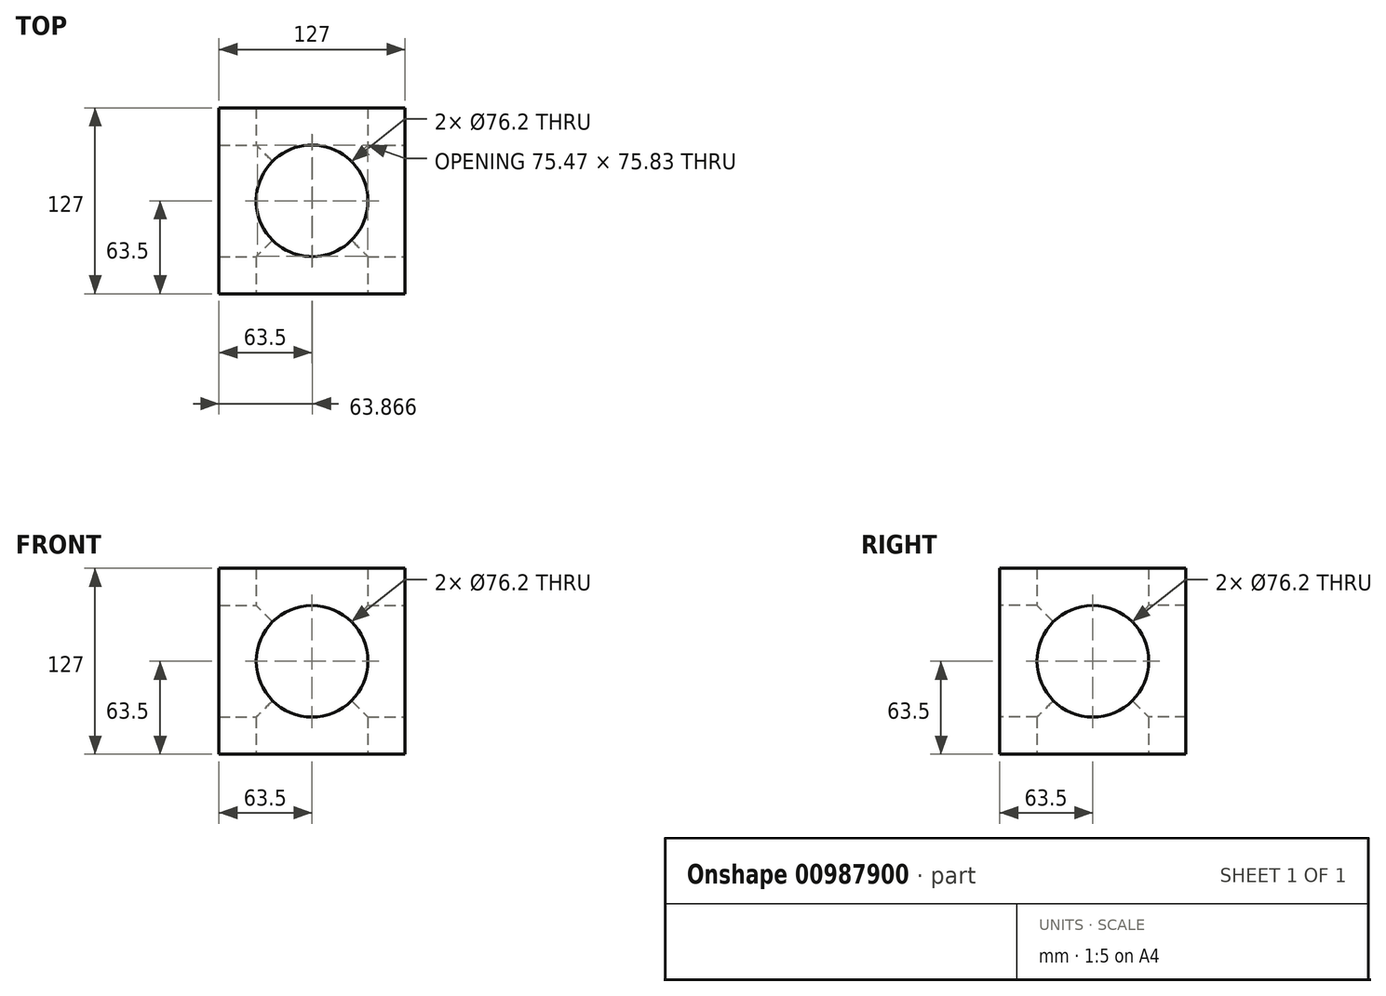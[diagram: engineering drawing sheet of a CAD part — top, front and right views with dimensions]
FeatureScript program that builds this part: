
annotation { "Feature Type Name" : "Feature", "Feature Type Description" : "" }
export const myFeature = defineFeature(function(context is Context, id is Id, definition is map)
    precondition{}
    {
        {
            var Q0;
            Q0=qCreatedBy(makeId("Top.planeOp"),FACE);
            var sketch = newSketch(context, id + "F0", { "sketchPlane" : qUnion([Q0])});
            skLineSegment(sketch, "E0.bottom", {"start": v(63.5, -63.5) * mm, "end": v(-63.5, -63.5) * mm});
            skLineSegment(sketch, "E0.top", {"start": v(63.5, 63.5) * mm, "end": v(-63.5, 63.5) * mm});
            skLineSegment(sketch, "E0.left", {"start": v(63.5, -63.5) * mm, "end": v(63.5, 63.5) * mm});
            skLineSegment(sketch, "E0.right", {"start": v(-63.5, -63.5) * mm, "end": v(-63.5, 63.5) * mm});
            skPoint(sketch, "E0.middle", {"position": v(0, 0) * mm});
            skSolve(sketch);
        }
        {
            var Q0;
            Q0=makeQuery(id+"F0.imprint","IMPRINT",FACE,{"disambiguationData":[TD([[makeQuery(id+"F0.imprint","IMPRINT",EDGE,{"derivedFrom":sQuery(id+"F0.wireOp",EDGE,"E0.bottom")}),-1.0]])]});
            extrude(context, id + "F1", {"entities" : qUnion([Q0]), "endBound" : BoundingType.SYMMETRIC, "depth" : 127 * mm, "offsetDistance" : 25.4 * mm});
        }
        {
            var Q0;
            Q0=qCreatedBy(makeId("Top.planeOp"),FACE);
            var sketch = newSketch(context, id + "F2", { "sketchPlane" : qUnion([Q0])});
            skCircle(sketch, "E1", {"center": v(0, 0) * mm, "radius": 38.1 * mm});
            skSolve(sketch);
        }
        {
            var Q0;
            Q0 = qSketchRegion(id + "F2", true);
            extrude(context, id + "F3", {"entities" : qUnion([Q0]), "operationType" : NewBodyOperationType.REMOVE, "endBound" : BoundingType.SYMMETRIC, "depth" : 127 * mm, "offsetDistance" : 25.4 * mm});
        }
        {
            var Q0;
            Q0=qCreatedBy(makeId("Front.planeOp"),FACE);
            var sketch = newSketch(context, id + "F4", { "sketchPlane" : qUnion([Q0])});
            skCircle(sketch, "E2", {"center": v(0, 0) * mm, "radius": 38.1 * mm});
            skSolve(sketch);
        }
        {
            var Q0;
            Q0 = qSketchRegion(id + "F4", true);
            extrude(context, id + "F5", {"entities" : qUnion([Q0]), "operationType" : NewBodyOperationType.REMOVE, "endBound" : BoundingType.SYMMETRIC, "oppositeDirection" : true, "depth" : 127 * mm, "offsetDistance" : 25.4 * mm});
        }
        {
            var Q0;
            Q0=qCreatedBy(makeId("Right.planeOp"),FACE);
            var sketch = newSketch(context, id + "F6", { "sketchPlane" : qUnion([Q0])});
            skCircle(sketch, "E3", {"center": v(0, 0) * mm, "radius": 38.1 * mm});
            skSolve(sketch);
        }
        {
            var Q0;
            Q0 = qSketchRegion(id + "F6", true);
            extrude(context, id + "F7", {"entities" : qUnion([Q0]), "operationType" : NewBodyOperationType.REMOVE, "endBound" : BoundingType.SYMMETRIC, "oppositeDirection" : true, "depth" : 127 * mm, "offsetDistance" : 25.4 * mm});
        }
    });
